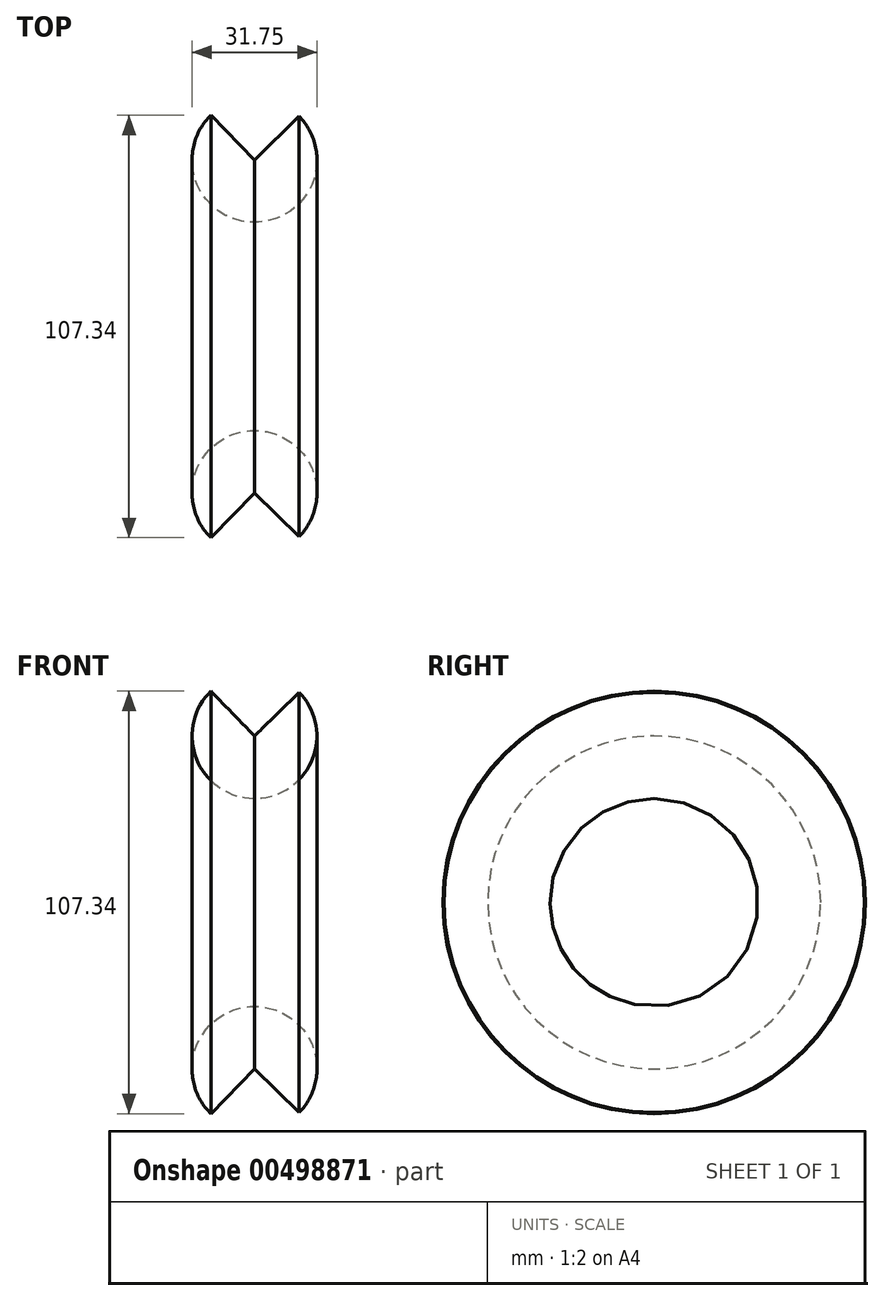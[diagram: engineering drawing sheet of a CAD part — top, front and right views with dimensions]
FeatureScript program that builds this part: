
annotation { "Feature Type Name" : "Feature", "Feature Type Description" : "" }
export const myFeature = defineFeature(function(context is Context, id is Id, definition is map)
    precondition{}
    {
        {
            var Q0;
            Q0=qCreatedBy(makeId("Front.planeOp"),FACE);
            var sketch = newSketch(context, id + "F0", { "sketchPlane" : qUnion([Q0])});
            skCircle(sketch, "E0", {"center": v(-14.1, 40) * mm, "radius": 15.88 * mm});
            skLineSegment(sketch, "E1", {"start": v(-14.1, 40) * mm, "end": v(-25.19, 51.37) * mm});
            skLineSegment(sketch, "E2.1.0", {"start": v(-14.1, 40) * mm, "end": v(-29.98, 40.2) * mm});
            skLineSegment(sketch, "E2.2.0", {"start": v(-14.1, 40) * mm, "end": v(-25.46, 28.92) * mm});
            skLineSegment(sketch, "E2.3.0", {"start": v(-14.1, 40) * mm, "end": v(-14.3, 24.13) * mm});
            skLineSegment(sketch, "E2.4.0", {"start": v(-14.1, 40) * mm, "end": v(-3.02, 28.64) * mm});
            skLineSegment(sketch, "E2.5.0", {"start": v(-14.1, 40) * mm, "end": v(1.77, 39.81) * mm});
            skLineSegment(sketch, "E2.6.0", {"start": v(-14.1, 40) * mm, "end": v(-2.74, 51.1) * mm});
            skLineSegment(sketch, "E2.7.0", {"start": v(-14.1, 40) * mm, "end": v(-13.9, 55.88) * mm});
            skLineSegment(sketch, "E3", {"start": v(-14.3, 24.13) * mm, "end": v(-14.3, -2.3) * mm});
            skPoint(sketch, "E4", {"position": v(-14.3, -2.3) * mm});
            skLineSegment(sketch, "E5", {"start": v(-14.3, -2.3) * mm, "end": v(14.1, -2.3) * mm});
            skSolve(sketch);
        }
        {
            var Q0;
            {var subQ0=sQuery(id+"F0.wireOp",EDGE,"E2.3.0");Q0=makeQuery(id+"F0.imprint","IMPRINT",FACE,{"disambiguationData":[TD([[makeQuery(id+"F0.imprint","IMPRINT",EDGE,{"derivedFrom":subQ0}),1.0]])]});}
            var Q1;
            {var subQ0=sQuery(id+"F0.wireOp",EDGE,"E2.2.0");Q1=makeQuery(id+"F0.imprint","IMPRINT",FACE,{"disambiguationData":[TD([[makeQuery(id+"F0.imprint","IMPRINT",EDGE,{"derivedFrom":subQ0}),1.0]])]});}
            var Q2;
            {var subQ0=sQuery(id+"F0.wireOp",EDGE,"E1");Q2=makeQuery(id+"F0.imprint","IMPRINT",FACE,{"disambiguationData":[TD([[makeQuery(id+"F0.imprint","IMPRINT",EDGE,{"derivedFrom":subQ0}),1.0]])]});}
            var Q3;
            {var subQ0=sQuery(id+"F0.wireOp",EDGE,"E2.1.0");Q3=makeQuery(id+"F0.imprint","IMPRINT",FACE,{"disambiguationData":[TD([[makeQuery(id+"F0.imprint","IMPRINT",EDGE,{"derivedFrom":subQ0}),1.0]])]});}
            var Q4;
            {var subQ0=sQuery(id+"F0.wireOp",EDGE,"E2.4.0");Q4=makeQuery(id+"F0.imprint","IMPRINT",FACE,{"disambiguationData":[TD([[makeQuery(id+"F0.imprint","IMPRINT",EDGE,{"derivedFrom":subQ0}),1.0]])]});}
            var Q5;
            {var subQ0=sQuery(id+"F0.wireOp",EDGE,"E2.5.0");Q5=makeQuery(id+"F0.imprint","IMPRINT",FACE,{"disambiguationData":[TD([[makeQuery(id+"F0.imprint","IMPRINT",EDGE,{"derivedFrom":subQ0}),1.0]])]});}
            var Q6;
            Q6=sQuery(id+"F0.wireOp",EDGE,"E5");
            revolve(context, id + "F1", {"entities" : qUnion([Q0, Q1, Q2, Q3, Q4, Q5]), "axis" : qUnion([Q6]), "revolveType" : RevolveType.FULL});
        }
    });
